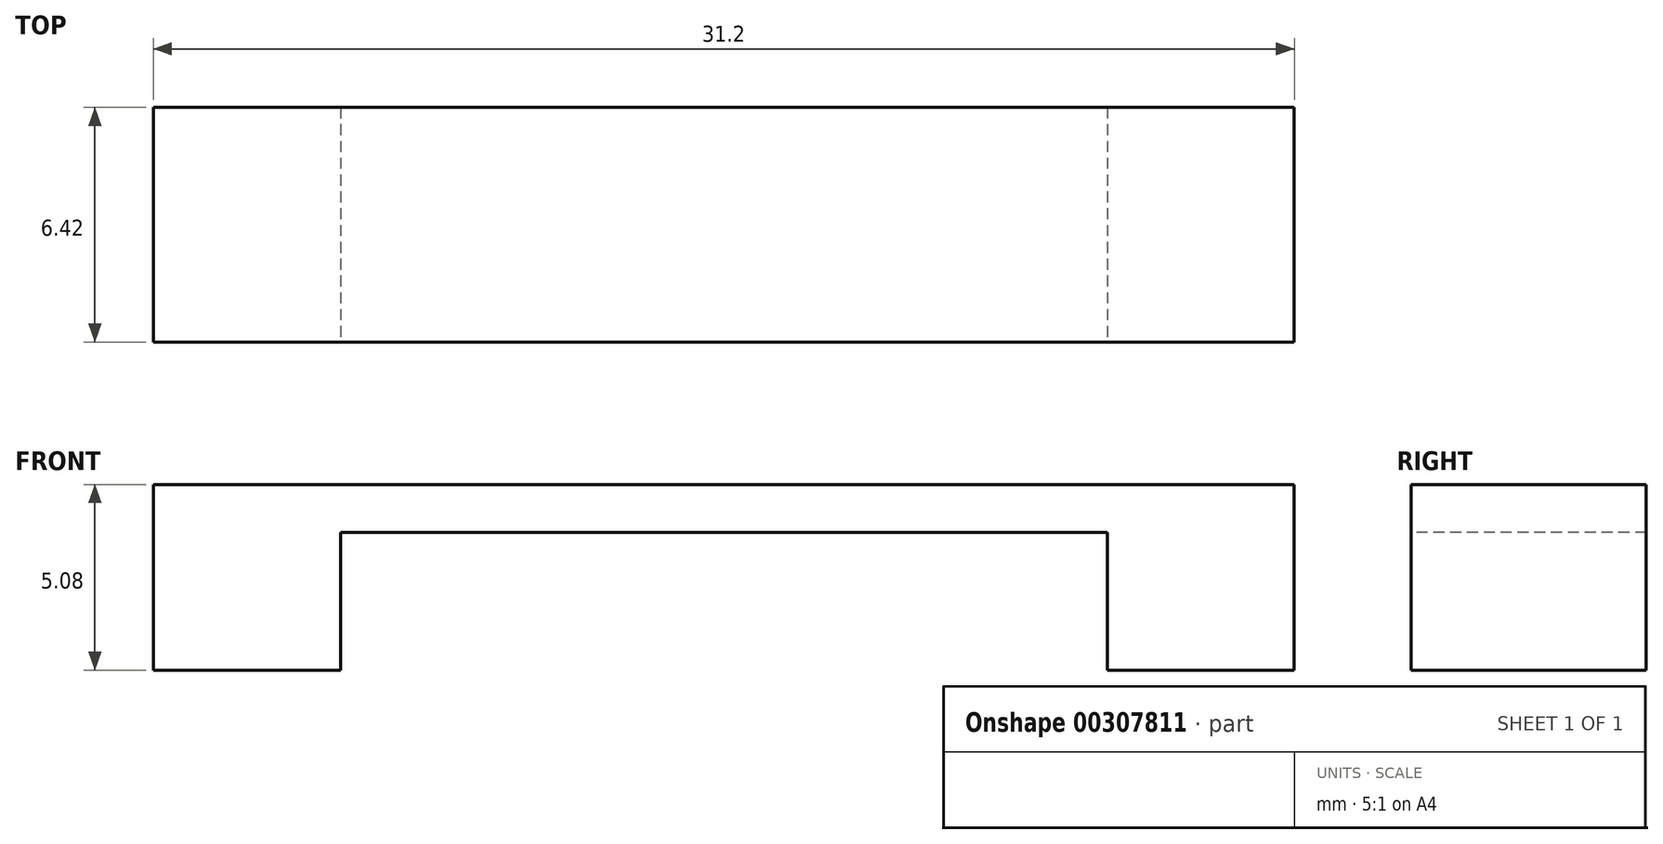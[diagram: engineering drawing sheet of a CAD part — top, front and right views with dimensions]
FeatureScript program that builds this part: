
annotation { "Feature Type Name" : "Feature", "Feature Type Description" : "" }
export const myFeature = defineFeature(function(context is Context, id is Id, definition is map)
    precondition{}
    {
        {
            var Q0;
            Q0=qCreatedBy(makeId("Top.planeOp"),FACE);
            var sketch = newSketch(context, id + "F0", { "sketchPlane" : qUnion([Q0])});
            skLineSegment(sketch, "E0.bottom", {"start": v(15.6, 3.21) * mm, "end": v(-15.6, 3.21) * mm});
            skLineSegment(sketch, "E0.top", {"start": v(15.6, -3.21) * mm, "end": v(-15.6, -3.21) * mm});
            skLineSegment(sketch, "E0.left", {"start": v(15.6, 3.21) * mm, "end": v(15.6, -3.21) * mm});
            skLineSegment(sketch, "E0.right", {"start": v(-15.6, 3.21) * mm, "end": v(-15.6, -3.21) * mm});
            skPoint(sketch, "E0.middle", {"position": v(0, 0) * mm});
            skSolve(sketch);
        }
        {
            var Q0;
            Q0 = qSketchRegion(id + "F0", true);
            extrude(context, id + "F1", {"entities" : qUnion([Q0]), "depth" : 5.08 * mm});
        }
        {
            var Q0;
            Q0=makeQuery(id+"F1.opExtrude","SWEPT_FACE",FACE,{"disambiguationData":[OSD([sQuery(id+"F0.wireOp",EDGE,"E0.top")])]});
            var sketch = newSketch(context, id + "F2", { "sketchPlane" : qUnion([Q0])});
            skLineSegment(sketch, "E1.bottom", {"start": v(10.48, 3.77) * mm, "end": v(-10.48, 3.77) * mm});
            skLineSegment(sketch, "E1.top", {"start": v(10.48, -3.77) * mm, "end": v(-10.48, -3.77) * mm});
            skLineSegment(sketch, "E1.left", {"start": v(10.48, 3.77) * mm, "end": v(10.48, -3.77) * mm});
            skLineSegment(sketch, "E1.right", {"start": v(-10.48, 3.77) * mm, "end": v(-10.48, -3.77) * mm});
            skPoint(sketch, "E1.middle", {"position": v(0, 0) * mm});
            skSolve(sketch);
        }
        {
            var Q0;
            {var subQ0=sQuery(id+"F2.wireOp",EDGE,"E1.bottom");Q0=makeQuery(id+"F2.imprint","IMPRINT",FACE,{"disambiguationData":[TD([[makeQuery(id+"F2.imprint","IMPRINT",EDGE,{"derivedFrom":subQ0}),1.0]])]});}
            extrude(context, id + "F3", {"entities" : qUnion([Q0]), "operationType" : NewBodyOperationType.REMOVE, "endBound" : BoundingType.THROUGH_ALL, "oppositeDirection" : true, "depth" : 25.4 * mm});
        }
    });
